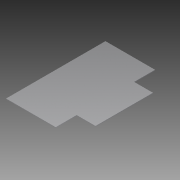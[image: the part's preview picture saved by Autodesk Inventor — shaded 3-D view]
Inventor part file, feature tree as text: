
AUTODESK INVENTOR PART (.ipt)
format: ipt  version: 2015 (Build 190159000, 159)  size: 95,744 bytes
history: native  units: in
note: dims shown in document units (in); Inventor stores cm internally (conversion verified against a paired STEP export)
features: extrude x1, sketch x1
ambient origin geometry x8: Origin, YZ Plane, XZ Plane, XY Plane, X Axis, Y Axis, Z Axis, Center Point
bodies: Solid1 (feature_tree)
feature tree (2):
  extrude  "Extrusion1"  Depth=14.0in
  sketch  "Sketch1"  dims[d0=9.6457in d1=14.0in d2=2.6575in d3=2.9528in d4=2.657in d5=2.953in d6=0.0984in d7=0.0in]
